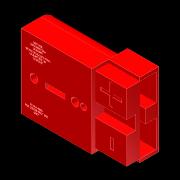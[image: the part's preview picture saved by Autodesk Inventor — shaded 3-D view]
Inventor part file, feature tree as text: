
AUTODESK INVENTOR PART (.ipt)
format: ipt  version: 2012 (Build 160160000, 160)  size: 1,669,120 bytes
history: native  units: in
note: dims shown in document units (in); Inventor stores cm internally (conversion verified against a paired STEP export)
features: sketch x21, extrude x17, hole x2, fillet x2
ambient origin geometry x8: Origin, YZ Plane, XZ Plane, XY Plane, X Axis, Y Axis, Z Axis, Center Point
bodies: Solid1 (feature_tree)
feature tree (42):
  extrude  "Extrusion1"  Depth=1.372in
  hole  "Hole1"  [1 undecoded]
  hole  "Hole2"  [1 undecoded]
  extrude  "Extrusion2"  Depth=0.152in
  extrude  "Extrusion3"  Depth=0.087in
  fillet  "Fillet1"  Radius=0.365in
  extrude  "Extrusion6"  Depth=0.288in
  extrude  "Extrusion7"  Depth=0.3in
  extrude  "Extrusion8"  Depth=0.58in TaperAngle=0.0deg
  extrude  "Extrusion9"  Depth=0.245in
  extrude  "Extrusion10"  Depth=0.063in
  extrude  "Extrusion11"  Depth=0.255in
  extrude  "Extrusion12"  Depth=1.246in
  extrude  "Extrusion13"  Depth=0.063in
  extrude  "Extrusion14"  Depth=0.05in
  fillet  "Fillet2"  Radius=0.505in
  extrude  "Extrusion15"  Depth=0.2938in
  extrude  "Extrusion16"  Depth=0.578in TaperAngle=0.0deg
  extrude  "Extrusion17"  Depth=0.578in TaperAngle=0.0deg
  extrude  "Extrusion18"  Depth=0.578in TaperAngle=0.0deg
  extrude  "Extrusion19"  Depth=0.444in
  sketch  "Sketch22"  dims[d78=0.005in d79=0.0in]
  sketch  "Sketch23"  dims[d80=1.0in d81=0.0in d82=0.2in d83=0.001in d84=0.0in d85=0.01in d86=0.0in d87=0.01in d88=0.0in d89=0.05in d90=0.0in d91=0.001in d92=0.0in]
  sketch  "Sketch1"  dims[d0=1.31in d1=1.372in]
  sketch  "Sketch2"  dims[d2=0.661in d3=0.0in d4=0.238in]
  sketch  "Sketch3"  dims[d5=1.0in d6=1.161in]
  sketch  "Sketch4"  dims[d7=0.148in d8=0.5in d9=0.375in d10=0.25in d11=0.5635in d12=0.75in d13=0.8108in d14=0.152in]
  sketch  "Sketch5"  dims[d15=0.118in d16=0.5in d17=0.375in d18=0.25in d19=0.5635in d20=0.27in d21=0.0in d22=0.087in d23=0.365in]
  sketch  "Sketch8"  dims[d24=0.436in d25=0.0in d26=0.288in]
  sketch  "Sketch9"  dims[d27=0.093in d28=0.0in d29=0.3in]
  sketch  "Sketch10"  dims[d46=0.066in d47=0.58in d48=0.0in]
  sketch  "Sketch11"  dims[d49=0.063in d50=0.245in]
  sketch  "Sketch12"  dims[d51=0.245in d52=0.063in]
  sketch  "Sketch13"  dims[d53=0.58in d54=0.0in d55=0.255in]
  sketch  "Sketch14"  dims[d56=0.167in d57=1.246in]
  sketch  "Sketch15"  dims[d58=0.58in d59=0.0in d60=0.063in]
  sketch  "Sketch16"  dims[d61=0.05in d62=0.05in d63=0.505in]
  sketch  "Sketch17"  dims[d64=0.505in d65=0.2938in]
  sketch  "Sketch18"  dims[d66=0.3in d67=0.578in d68=0.0in]
  sketch  "Sketch19"  dims[d69=0.102in d70=0.578in d71=0.0in]
  sketch  "Sketch20"  dims[d72=0.578in d73=0.0in d74=0.578in d75=0.0in]
  sketch  "Sketch21"  dims[d76=0.444in d77=0.444in]
note: 2 required parameter values undecoded (feature->parameter linkage not recoverable at this tier; creation-order binding heuristic only, values carry confidence <= 0.55)
